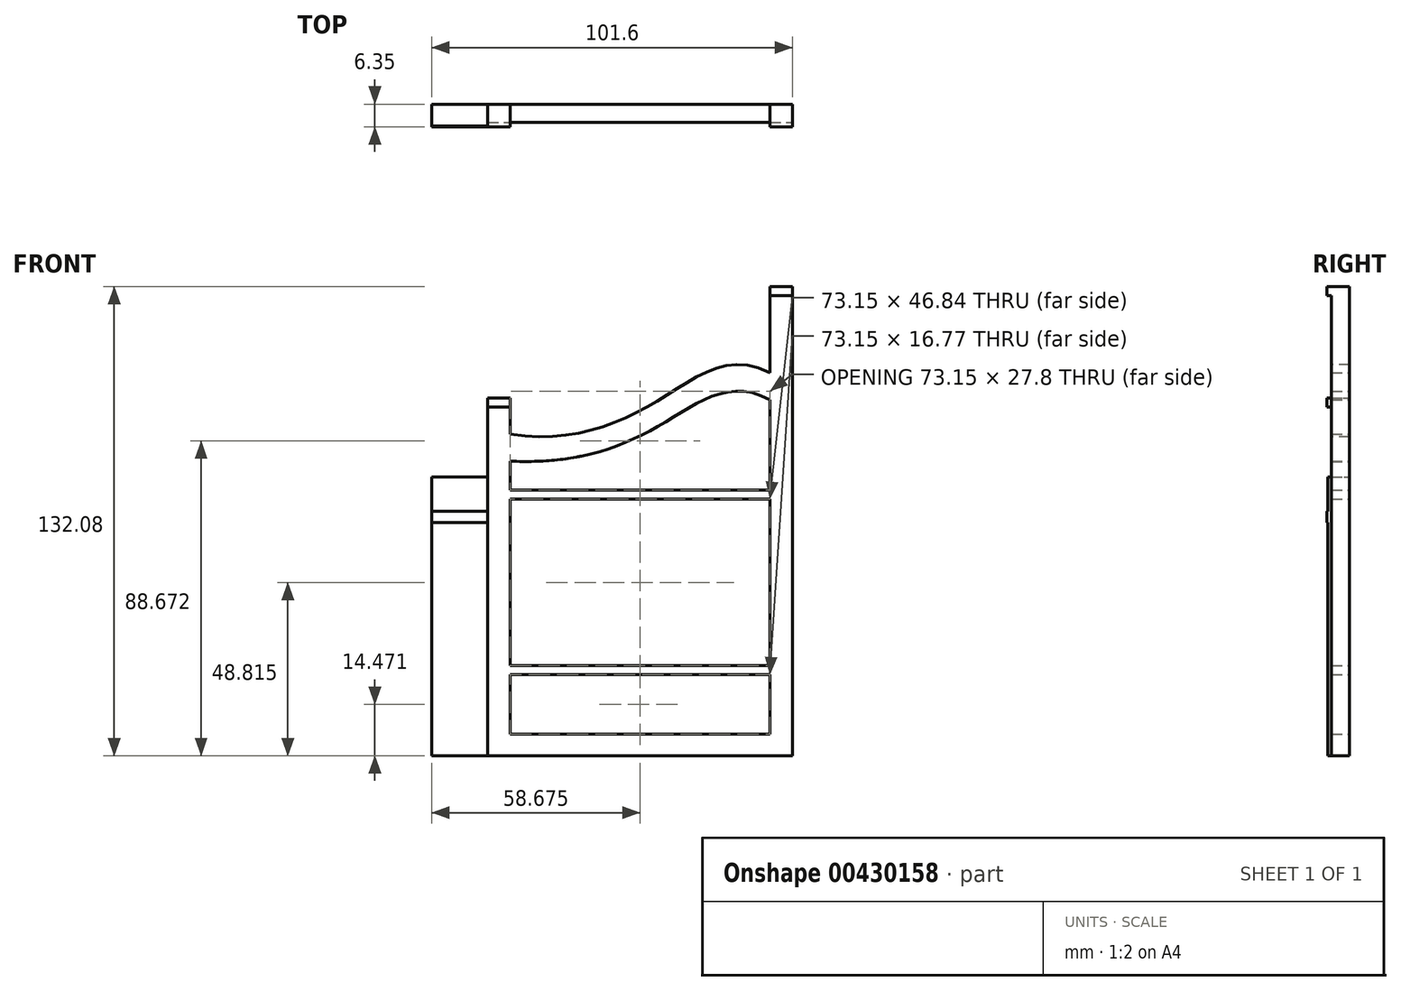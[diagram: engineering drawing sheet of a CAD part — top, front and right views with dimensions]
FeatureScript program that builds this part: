
annotation { "Feature Type Name" : "Feature", "Feature Type Description" : "" }
export const myFeature = defineFeature(function(context is Context, id is Id, definition is map)
    precondition{}
    {
        {
            var Q0;
            Q0=qCreatedBy(makeId("Front.planeOp"),FACE);
            var sketch = newSketch(context, id + "F0", { "sketchPlane" : qUnion([Q0])});
            skLineSegment(sketch, "E0.bottom", {"start": v(-83.48, 46.1) * mm, "end": v(-67.73, 46.1) * mm});
            skLineSegment(sketch, "E0.top", {"start": v(-83.48, -32.38) * mm, "end": v(-67.73, -32.38) * mm});
            skLineSegment(sketch, "E0.left", {"start": v(-83.48, 46.1) * mm, "end": v(-83.48, -32.38) * mm});
            skLineSegment(sketch, "E0.right", {"start": v(-67.73, 46.1) * mm, "end": v(-67.73, -32.38) * mm});
            skLineSegment(sketch, "E1.bottom", {"start": v(-67.73, 68.33) * mm, "end": v(-61.38, 68.33) * mm});
            skLineSegment(sketch, "E1.top", {"start": v(-67.73, -32.38) * mm, "end": v(-61.38, -32.38) * mm});
            skLineSegment(sketch, "E1.left", {"start": v(-67.73, 68.33) * mm, "end": v(-67.73, -32.38) * mm});
            skLineSegment(sketch, "E1.right", {"start": v(-61.38, 68.33) * mm, "end": v(-61.38, -32.38) * mm});
            skLineSegment(sketch, "E2.bottom", {"start": v(11.77, 99.7) * mm, "end": v(18.12, 99.7) * mm});
            skLineSegment(sketch, "E2.top", {"start": v(11.77, -32.38) * mm, "end": v(18.12, -32.38) * mm});
            skLineSegment(sketch, "E2.left", {"start": v(11.77, 99.7) * mm, "end": v(11.77, -32.38) * mm});
            skLineSegment(sketch, "E2.right", {"start": v(18.12, 99.7) * mm, "end": v(18.12, -32.38) * mm});
            skLineSegment(sketch, "E3.left", {"start": v(-61.38, 58.2) * mm, "end": v(-61.38, 42.97) * mm});
            skLineSegment(sketch, "E3.right", {"start": v(11.77, 75.41) * mm, "end": v(11.77, 46.1) * mm});
            skFitSpline(sketch, "E4", {"points": [v(-61.38, 58.2) * mm, v(-18.64, 68.33) * mm, v(11.77, 75.41) * mm], "startDerivative": vector(96.97, -15.79) * mm, "endDerivative": vector(77.2, -40.21) * mm});
            skFitSpline(sketch, "E5", {"points": [v(-61.38, 50.59) * mm, v(-19.43, 60.57) * mm, v(11.77, 67.8) * mm], "startDerivative": vector(97, -4.8) * mm, "endDerivative": vector(75.65, -43.06) * mm});
            skLineSegment(sketch, "E6.bottom", {"start": v(-61.38, -32.38) * mm, "end": v(-61.38, -32.38) * mm});
            skLineSegment(sketch, "E6.top", {"start": v(-61.38, -26.3) * mm, "end": v(-61.38, -26.3) * mm});
            skLineSegment(sketch, "E6.left", {"start": v(-61.38, -32.38) * mm, "end": v(-61.38, -26.3) * mm});
            skLineSegment(sketch, "E6.right", {"start": v(-61.38, -32.38) * mm, "end": v(-61.38, -26.3) * mm});
            skLineSegment(sketch, "E7.bottom", {"start": v(-61.38, -26.3) * mm, "end": v(11.77, -26.3) * mm});
            skLineSegment(sketch, "E7.top", {"start": v(-61.38, -32.38) * mm, "end": v(11.77, -32.38) * mm});
            skLineSegment(sketch, "E7.left", {"start": v(-61.38, -26.3) * mm, "end": v(-61.38, -32.38) * mm});
            skLineSegment(sketch, "E7.right", {"start": v(11.77, -26.3) * mm, "end": v(11.77, -32.38) * mm});
            skLineSegment(sketch, "E8", {"start": v(-61.38, 10.16) * mm, "end": v(11.77, 10.16) * mm});
            skLineSegment(sketch, "E9", {"start": v(-61.38, 0) * mm, "end": v(11.77, 0) * mm});
            skLineSegment(sketch, "E10", {"start": v(-83.48, 33.34) * mm, "end": v(-67.73, 33.34) * mm});
            skLineSegment(sketch, "E11", {"start": v(-67.73, 33.34) * mm, "end": v(-67.73, 36.48) * mm});
            skLineSegment(sketch, "E12", {"start": v(-67.73, 36.48) * mm, "end": v(-83.48, 36.48) * mm});
            skLineSegment(sketch, "E13", {"start": v(-83.48, 36.48) * mm, "end": v(-83.48, 33.34) * mm});
            skLineSegment(sketch, "E14", {"start": v(-67.73, 68.33) * mm, "end": v(-67.73, 65.79) * mm});
            skLineSegment(sketch, "E15", {"start": v(-67.73, 65.79) * mm, "end": v(-61.38, 65.79) * mm});
            skLineSegment(sketch, "E16", {"start": v(-61.38, 65.79) * mm, "end": v(-61.38, 68.33) * mm});
            skLineSegment(sketch, "E17", {"start": v(11.77, 99.7) * mm, "end": v(11.77, 97.16) * mm});
            skLineSegment(sketch, "E18", {"start": v(11.77, 97.16) * mm, "end": v(18.12, 97.16) * mm});
            skLineSegment(sketch, "E19", {"start": v(18.12, 97.16) * mm, "end": v(18.12, 99.7) * mm});
            skLineSegment(sketch, "E20", {"start": v(-61.38, 12.06) * mm, "end": v(11.77, 12.07) * mm});
            skLineSegment(sketch, "E21", {"start": v(-61.38, -1.9) * mm, "end": v(11.77, -1.9) * mm});
            skPoint(sketch, "E22", {"position": v(18.12, 12.06) * mm});
            skPoint(sketch, "E23", {"position": v(18.12, 10.16) * mm});
            skPoint(sketch, "E24", {"position": v(18.12, 0) * mm});
            skPoint(sketch, "E25", {"position": v(18.12, -1.9) * mm});
            skLineSegment(sketch, "E26", {"start": v(-61.38, 11.11) * mm, "end": v(11.77, 11.11) * mm});
            skLineSegment(sketch, "E27", {"start": v(-61.38, -0.95) * mm, "end": v(11.77, -0.95) * mm});
            skLineSegment(sketch, "E28", {"start": v(-61.38, 42.4) * mm, "end": v(11.77, 42.4) * mm});
            skLineSegment(sketch, "E29", {"start": v(-61.38, 39.85) * mm, "end": v(11.77, 39.85) * mm});
            skLineSegment(sketch, "E30", {"start": v(-61.38, -6.98) * mm, "end": v(11.77, -6.98) * mm});
            skLineSegment(sketch, "E31", {"start": v(-61.38, -9.52) * mm, "end": v(11.77, -9.52) * mm});
            skLineSegment(sketch, "E32", {"start": v(-42.84, 51.7) * mm, "end": v(-42.84, -26.3) * mm});
            skLineSegment(sketch, "E33", {"start": v(-42.84, -26.3) * mm, "end": v(-41.31, -26.3) * mm});
            skLineSegment(sketch, "E34", {"start": v(-41.31, -26.3) * mm, "end": v(-41.31, 52) * mm});
            skLineSegment(sketch, "E35", {"start": v(11.77, 17.97) * mm, "end": v(11.77, 19.24) * mm});
            skLineSegment(sketch, "E36", {"start": v(-61.38, 21) * mm, "end": v(11.77, 21) * mm});
            skLineSegment(sketch, "E37", {"start": v(11.77, 21) * mm, "end": v(11.77, 22.27) * mm});
            skLineSegment(sketch, "E38", {"start": v(11.77, 22.27) * mm, "end": v(-61.38, 22.27) * mm});
            skSolve(sketch);
        }
        {
            var Q0;
            {var subQ0=sQuery(id+"F0.wireOp",EDGE,"E4");Q0=makeQuery(id+"F0.imprint","IMPRINT",FACE,{"disambiguationData":[TD([[makeQuery(id+"F0.imprint","IMPRINT",EDGE,{"derivedFrom":subQ0}),-1.0]])]});}
            var Q1;
            {var subQ16=sQuery(id+"F0.wireOp",EDGE,"E1.top");Q1=makeQuery(id+"F0.imprint","IMPRINT",FACE,{"disambiguationData":[TD([[makeQuery(id+"F0.imprint","IMPRINT",EDGE,{"derivedFrom":subQ16}),1.0]])]});}
            var Q2;
            Q2=makeQuery(id+"F0.imprint","IMPRINT",FACE,{"disambiguationData":[TD([[makeQuery(id+"F0.imprint","IMPRINT",EDGE,{"derivedFrom":sQuery(id+"F0.wireOp",EDGE,"E7.top")}),1.0]])]});
            var Q3;
            Q3=makeQuery(id+"F0.imprint","IMPRINT",FACE,{"disambiguationData":[TD([[makeQuery(id+"F0.imprint","IMPRINT",EDGE,{"derivedFrom":sQuery(id+"F0.wireOp",EDGE,"E2.top")}),1.0]])]});
            var Q4;
            {var subQ0=sQuery(id+"F0.wireOp",EDGE,"E32");var subQ1=sQuery(id+"F0.wireOp",EDGE,"E30");var subQ2=makeQuery(id+"F0.imprint","INTERSECT",VERTEX,{"derivedFrom":[subQ1,subQ0]});Q4=makeQuery(id+"F0.imprint","IMPRINT",FACE,{"disambiguationData":[TD([[makeQuery(id+"F0.imprint","IMPRINT",EDGE,{"disambiguationData":[TD([[subQ2,-1.0]])],"derivedFrom":subQ1}),-1.0]])]});}
            var Q5;
            {var subQ0=sQuery(id+"F0.wireOp",EDGE,"E30");var subQ1=sQuery(id+"F0.wireOp",EDGE,"E1.right");var subQ2=makeQuery(id+"F0.imprint","INTERSECT",VERTEX,{"derivedFrom":[subQ1,subQ0]});Q5=makeQuery(id+"F0.imprint","IMPRINT",FACE,{"disambiguationData":[TD([[makeQuery(id+"F0.imprint","IMPRINT",EDGE,{"disambiguationData":[TD([[subQ2,-1.0]])],"derivedFrom":subQ1}),1.0]])]});}
            var Q6;
            {var subQ0=sQuery(id+"F0.wireOp",EDGE,"E30");var subQ1=sQuery(id+"F0.wireOp",EDGE,"E2.left");var subQ2=makeQuery(id+"F0.imprint","INTERSECT",VERTEX,{"derivedFrom":[subQ1,subQ0]});Q6=makeQuery(id+"F0.imprint","IMPRINT",FACE,{"disambiguationData":[TD([[makeQuery(id+"F0.imprint","IMPRINT",EDGE,{"disambiguationData":[TD([[subQ2,-1.0]])],"derivedFrom":subQ1}),-1.0]])]});}
            var Q7;
            {var subQ0=sQuery(id+"F0.wireOp",EDGE,"E28");var subQ1=sQuery(id+"F0.wireOp",EDGE,"E2.left");var subQ2=makeQuery(id+"F0.imprint","INTERSECT",VERTEX,{"derivedFrom":[subQ1,subQ0]});Q7=makeQuery(id+"F0.imprint","IMPRINT",FACE,{"disambiguationData":[TD([[makeQuery(id+"F0.imprint","IMPRINT",EDGE,{"disambiguationData":[TD([[subQ2,-1.0]])],"derivedFrom":subQ1}),-1.0]])]});}
            var Q8;
            {var subQ0=sQuery(id+"F0.wireOp",EDGE,"E28");var subQ1=sQuery(id+"F0.wireOp",EDGE,"E1.right");var subQ2=makeQuery(id+"F0.imprint","INTERSECT",VERTEX,{"derivedFrom":[subQ1,subQ0]});Q8=makeQuery(id+"F0.imprint","IMPRINT",FACE,{"disambiguationData":[TD([[makeQuery(id+"F0.imprint","IMPRINT",EDGE,{"disambiguationData":[TD([[subQ2,-1.0]])],"derivedFrom":subQ1}),1.0]])]});}
            var Q9;
            {var subQ0=sQuery(id+"F0.wireOp",EDGE,"E32");var subQ1=sQuery(id+"F0.wireOp",EDGE,"E28");var subQ2=makeQuery(id+"F0.imprint","INTERSECT",VERTEX,{"derivedFrom":[subQ1,subQ0]});Q9=makeQuery(id+"F0.imprint","IMPRINT",FACE,{"disambiguationData":[TD([[makeQuery(id+"F0.imprint","IMPRINT",EDGE,{"disambiguationData":[TD([[subQ2,-1.0]])],"derivedFrom":subQ1}),-1.0]])]});}
            extrude(context, id + "F1", {"entities" : qUnion([Q0, Q1, Q2, Q3, Q4, Q5, Q6, Q7, Q8, Q9]), "depth" : 5.08 * mm, "offsetDistance" : 25.4 * mm});
        }
        {
            var Q0;
            Q0=makeQuery(id+"F0.imprint","IMPRINT",FACE,{"disambiguationData":[TD([[makeQuery(id+"F0.imprint","IMPRINT",EDGE,{"derivedFrom":sQuery(id+"F0.wireOp",EDGE,"E1.bottom")}),-1.0]])]});
            var Q1;
            Q1=makeQuery(id+"F0.imprint","IMPRINT",FACE,{"disambiguationData":[TD([[makeQuery(id+"F0.imprint","IMPRINT",EDGE,{"derivedFrom":sQuery(id+"F0.wireOp",EDGE,"E2.bottom")}),-1.0]])]});
            var Q2;
            Q2=makeQuery(id+"F0.imprint","IMPRINT",FACE,{"disambiguationData":[TD([[makeQuery(id+"F0.imprint","IMPRINT",EDGE,{"derivedFrom":sQuery(id+"F0.wireOp",EDGE,"E10")}),1.0]])]});
            extrude(context, id + "F2", {"entities" : qUnion([Q0, Q1, Q2]), "operationType" : NewBodyOperationType.ADD, "depth" : 6.35 * mm});
        }
        {
            var Q0;
            {var subQ0=sQuery(id+"F0.wireOp",EDGE,"E0.bottom");Q0=makeQuery(id+"F0.imprint","IMPRINT",FACE,{"disambiguationData":[TD([[makeQuery(id+"F0.imprint","IMPRINT",EDGE,{"derivedFrom":subQ0}),-1.0]])]});}
            var Q1;
            {var subQ0=sQuery(id+"F0.wireOp",EDGE,"E0.top");Q1=makeQuery(id+"F0.imprint","IMPRINT",FACE,{"disambiguationData":[TD([[makeQuery(id+"F0.imprint","IMPRINT",EDGE,{"derivedFrom":subQ0}),1.0]])]});}
            extrude(context, id + "F3", {"entities" : qUnion([Q0, Q1]), "operationType" : NewBodyOperationType.ADD, "depth" : 6.1 * mm});
        }
        {
            var Q0;
            {var subQ0=sQuery(id+"F0.wireOp",EDGE,"E28");Q0=makeQuery(id+"F0.imprint","IMPRINT",FACE,{"disambiguationData":[TD([[makeQuery(id+"F0.imprint","IMPRINT",EDGE,{"derivedFrom":subQ0}),-1.0]])]});}
            extrude(context, id + "F4", {"entities" : qUnion([Q0]), "operationType" : NewBodyOperationType.REMOVE, "depth" : 5.08 * mm, "offsetDistance" : 25.4 * mm});
        }
        {
            var Q0;
            {var subQ0=sQuery(id+"F0.wireOp",EDGE,"E30");Q0=makeQuery(id+"F0.imprint","IMPRINT",FACE,{"disambiguationData":[TD([[makeQuery(id+"F0.imprint","IMPRINT",EDGE,{"derivedFrom":subQ0}),-1.0]])]});}
            extrude(context, id + "F5", {"entities" : qUnion([Q0]), "operationType" : NewBodyOperationType.REMOVE, "depth" : 5.08 * mm, "offsetDistance" : 25.4 * mm});
        }
        {
            var Q0;
            {var subQ0=sQuery(id+"F0.wireOp",EDGE,"E28");var subQ1=sQuery(id+"F0.wireOp",EDGE,"E2.left");var subQ2=makeQuery(id+"F0.imprint","INTERSECT",VERTEX,{"derivedFrom":[subQ1,subQ0]});Q0=makeQuery(id+"F0.imprint","IMPRINT",FACE,{"disambiguationData":[TD([[makeQuery(id+"F0.imprint","IMPRINT",EDGE,{"disambiguationData":[TD([[subQ2,-1.0]])],"derivedFrom":subQ1}),-1.0]])]});}
            var Q1;
            {var subQ0=sQuery(id+"F0.wireOp",EDGE,"E28");var subQ1=sQuery(id+"F0.wireOp",EDGE,"E1.right");var subQ2=makeQuery(id+"F0.imprint","INTERSECT",VERTEX,{"derivedFrom":[subQ1,subQ0]});Q1=makeQuery(id+"F0.imprint","IMPRINT",FACE,{"disambiguationData":[TD([[makeQuery(id+"F0.imprint","IMPRINT",EDGE,{"disambiguationData":[TD([[subQ2,-1.0]])],"derivedFrom":subQ1}),1.0]])]});}
            var Q2;
            {var subQ0=sQuery(id+"F0.wireOp",EDGE,"E32");var subQ1=sQuery(id+"F0.wireOp",EDGE,"E28");var subQ2=makeQuery(id+"F0.imprint","INTERSECT",VERTEX,{"derivedFrom":[subQ1,subQ0]});Q2=makeQuery(id+"F0.imprint","IMPRINT",FACE,{"disambiguationData":[TD([[makeQuery(id+"F0.imprint","IMPRINT",EDGE,{"disambiguationData":[TD([[subQ2,-1.0]])],"derivedFrom":subQ1}),-1.0]])]});}
            var Q3;
            {var subQ0=sQuery(id+"F0.wireOp",EDGE,"E30");var subQ1=sQuery(id+"F0.wireOp",EDGE,"E1.right");var subQ2=makeQuery(id+"F0.imprint","INTERSECT",VERTEX,{"derivedFrom":[subQ1,subQ0]});Q3=makeQuery(id+"F0.imprint","IMPRINT",FACE,{"disambiguationData":[TD([[makeQuery(id+"F0.imprint","IMPRINT",EDGE,{"disambiguationData":[TD([[subQ2,-1.0]])],"derivedFrom":subQ1}),1.0]])]});}
            var Q4;
            {var subQ0=sQuery(id+"F0.wireOp",EDGE,"E30");var subQ1=sQuery(id+"F0.wireOp",EDGE,"E2.left");var subQ2=makeQuery(id+"F0.imprint","INTERSECT",VERTEX,{"derivedFrom":[subQ1,subQ0]});Q4=makeQuery(id+"F0.imprint","IMPRINT",FACE,{"disambiguationData":[TD([[makeQuery(id+"F0.imprint","IMPRINT",EDGE,{"disambiguationData":[TD([[subQ2,-1.0]])],"derivedFrom":subQ1}),-1.0]])]});}
            var Q5;
            {var subQ0=sQuery(id+"F0.wireOp",EDGE,"E32");var subQ1=sQuery(id+"F0.wireOp",EDGE,"E30");var subQ2=makeQuery(id+"F0.imprint","INTERSECT",VERTEX,{"derivedFrom":[subQ1,subQ0]});Q5=makeQuery(id+"F0.imprint","IMPRINT",FACE,{"disambiguationData":[TD([[makeQuery(id+"F0.imprint","IMPRINT",EDGE,{"disambiguationData":[TD([[subQ2,-1.0]])],"derivedFrom":subQ1}),-1.0]])]});}
            extrude(context, id + "F6", {"entities" : qUnion([Q0, Q1, Q2, Q3, Q4, Q5]), "operationType" : NewBodyOperationType.ADD, "depth" : 5.08 * mm, "offsetDistance" : 25.4 * mm});
        }
    });
